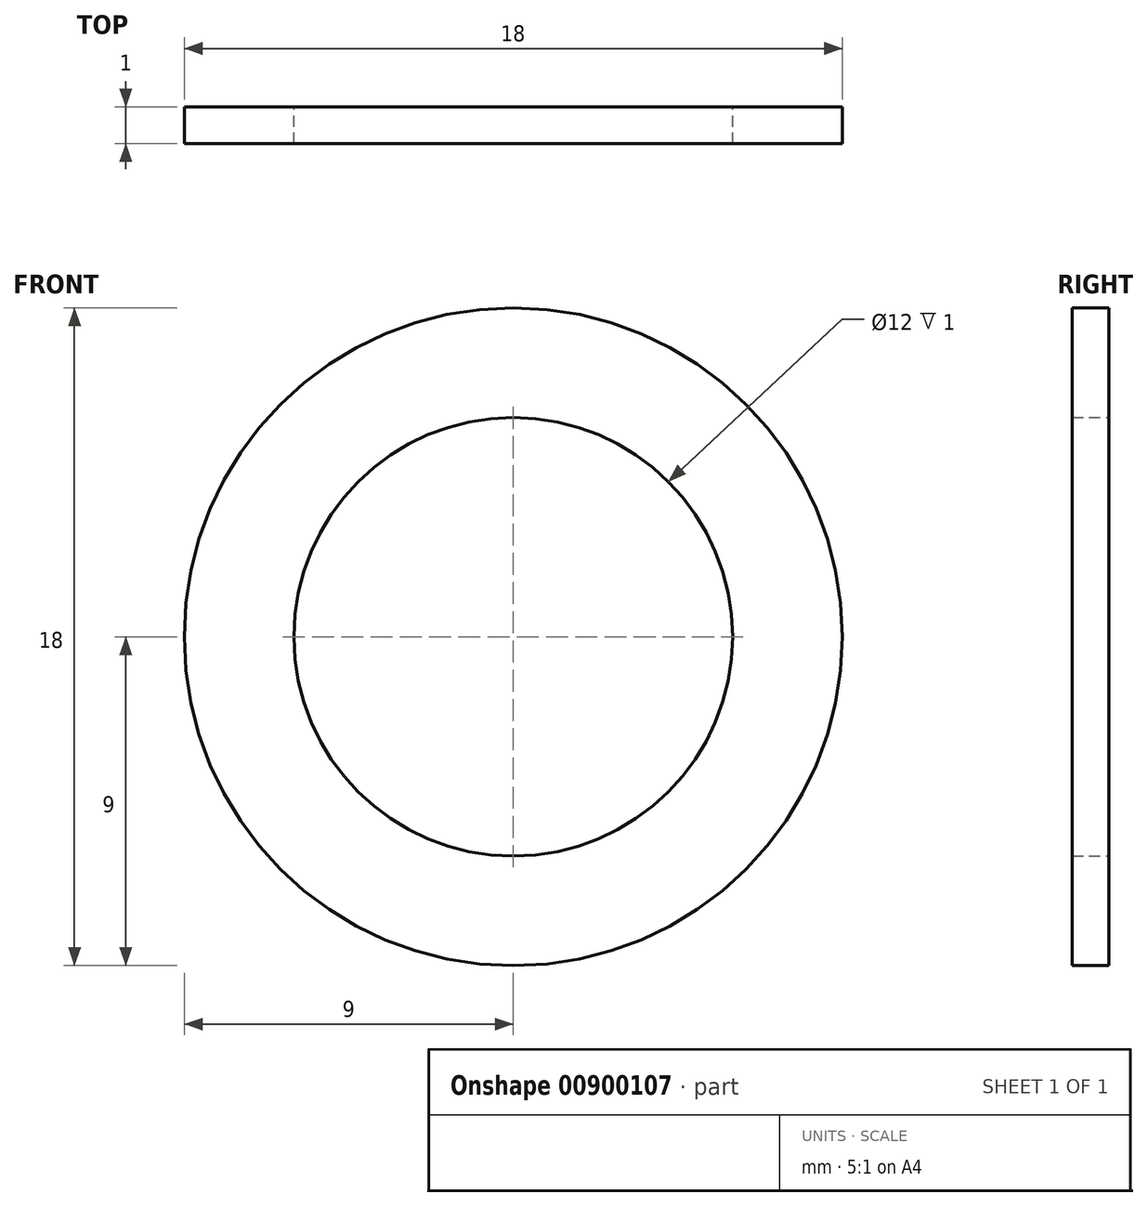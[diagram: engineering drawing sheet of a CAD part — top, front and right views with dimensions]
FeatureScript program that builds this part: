
annotation { "Feature Type Name" : "Feature", "Feature Type Description" : "" }
export const myFeature = defineFeature(function(context is Context, id is Id, definition is map)
    precondition{}
    {
        {
            var Q0;
            Q0=qCreatedBy(makeId("Front.planeOp"),FACE);
            var sketch = newSketch(context, id + "F0", { "sketchPlane" : qUnion([Q0])});
            skCircle(sketch, "E0", {"center": v(0, 0) * mm, "radius": 9 * mm});
            skCircle(sketch, "E1", {"center": v(0, 0) * mm, "radius": 6 * mm});
            skSolve(sketch);
        }
        {
            var Q0;
            Q0 = qSketchRegion(id + "F0", true);
            extrude(context, id + "F1", {"entities" : qUnion([Q0]), "depth" : 1 * mm, "offsetDistance" : 25 * mm});
        }
    });
